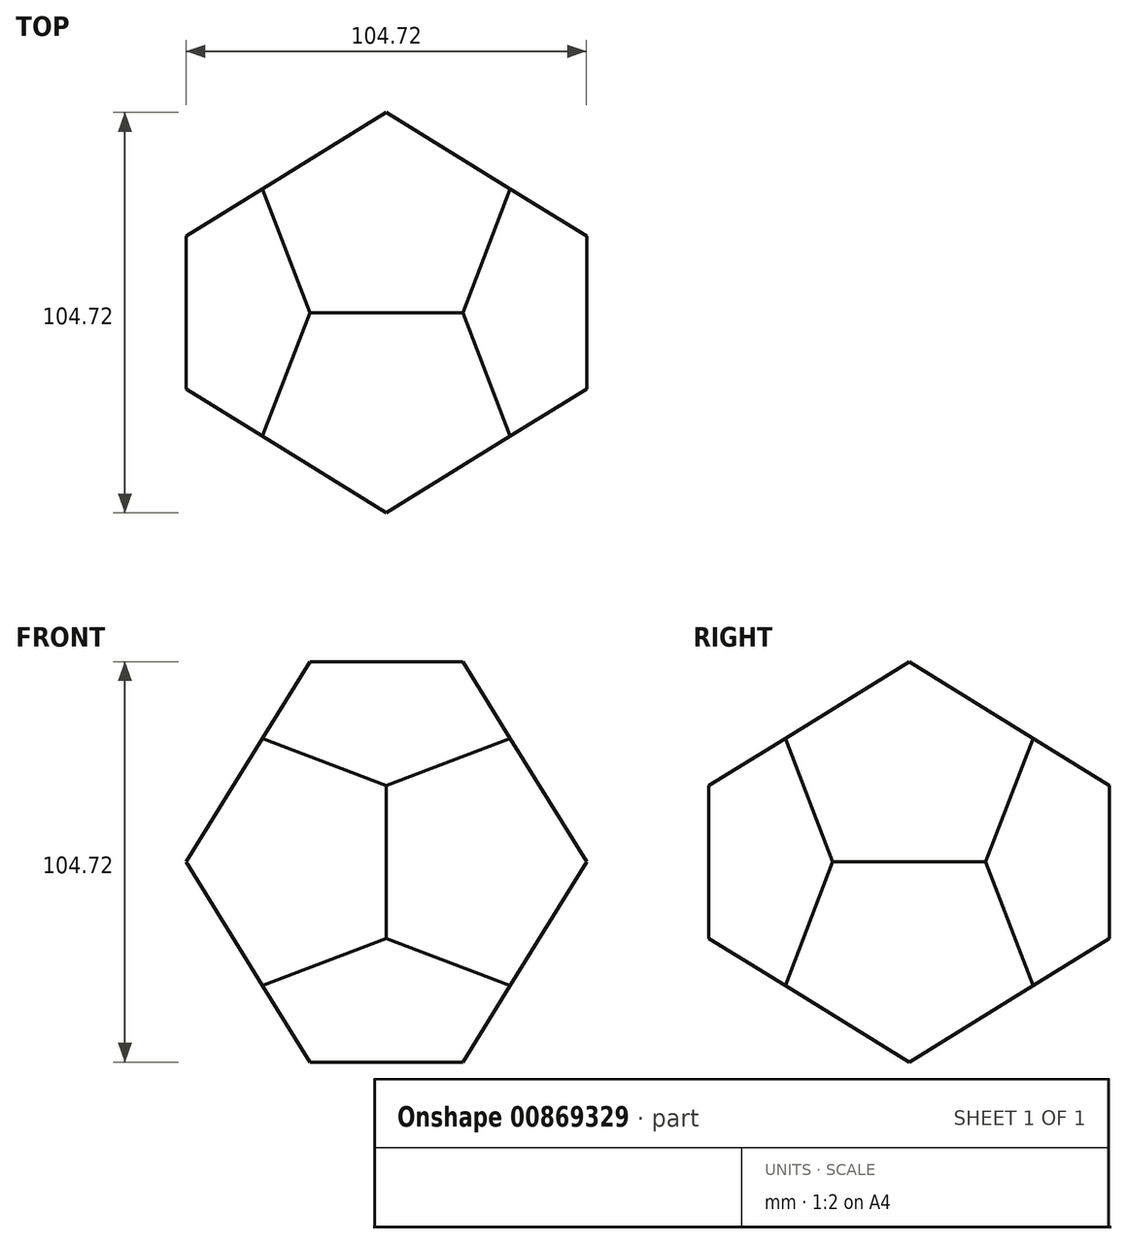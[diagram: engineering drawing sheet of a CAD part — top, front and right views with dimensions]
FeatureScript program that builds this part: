
annotation { "Feature Type Name" : "Feature", "Feature Type Description" : "" }
export const myFeature = defineFeature(function(context is Context, id is Id, definition is map)
    precondition{}
    {
        {
            assignVariable(context, id + "F0", {"name" : "lado", "anyValue" : 40});
        }
        {
            assignVariable(context, id + "F1", {"name" : "ladoSeccion", "anyValue" : (1 + sqrt(5)) / 2 * getVariable(context, 'lado')});
        }
        {
            var Q0;
            Q0=qCreatedBy(makeId("Top.planeOp"),FACE);
            var sketch = newSketch(context, id + "F2", { "sketchPlane" : qUnion([Q0])});
            skLineSegment(sketch, "E0.bottom", {"start": v(-32.36, 32.36) * mm, "end": v(32.36, 32.36) * mm});
            skLineSegment(sketch, "E0.top", {"start": v(-32.36, -32.36) * mm, "end": v(32.36, -32.36) * mm});
            skLineSegment(sketch, "E0.left", {"start": v(-32.36, 32.36) * mm, "end": v(-32.36, -32.36) * mm});
            skLineSegment(sketch, "E0.right", {"start": v(32.36, 32.36) * mm, "end": v(32.36, -32.36) * mm});
            skSolve(sketch);
        }
        {
            var Q0;
            Q0=makeQuery(id+"F2.imprint","IMPRINT",FACE,{"disambiguationData":[TD([[makeQuery(id+"F2.imprint","IMPRINT",EDGE,{"derivedFrom":sQuery(id+"F2.wireOp",EDGE,"E0.bottom")}),-1.0]])]});
            extrude(context, id + "F3", {"entities" : qUnion([Q0]), "depth" : (getVariable(context, 'ladoSeccion')) * mm, "offsetDistance" : 25 * mm, "symmetric" : true});
        }
        {
            var Q0;
            Q0=makeQuery(id+"F3.opExtrude","SWEPT_FACE",FACE,{"disambiguationData":[OSD([sQuery(id+"F2.wireOp",EDGE,"E0.bottom")])]});
            var sketch = newSketch(context, id + "F4", { "sketchPlane" : qUnion([Q0])});
            skLineSegment(sketch, "E1.0", {"start": v(32.36, 32.36) * mm, "end": v(-32.36, 32.36) * mm});
            skLineSegment(sketch, "E2.0", {"start": v(-32.36, 32.36) * mm, "end": v(-32.36, -32.36) * mm});
            skLineSegment(sketch, "E3.0", {"start": v(32.36, -32.36) * mm, "end": v(-32.36, -32.36) * mm});
            skLineSegment(sketch, "E4.0", {"start": v(32.36, 32.36) * mm, "end": v(32.36, -32.36) * mm});
            skLineSegment(sketch, "E5", {"start": v(-32.36, 32.36) * mm, "end": v(32.36, -32.36) * mm});
            skLineSegment(sketch, "E6", {"start": v(32.36, 32.36) * mm, "end": v(-32.36, -32.36) * mm});
            skPoint(sketch, "E7", {"position": v(0, 0) * mm});
            skSolve(sketch);
        }
        {
            var Q0;
            Q0=qCreatedBy(makeId("Right.planeOp"),FACE);
            var sketch = newSketch(context, id + "F5", { "sketchPlane" : qUnion([Q0])});
            skLineSegment(sketch, "E8.0", {"start": v(32.36, 32.36) * mm, "end": v(32.36, -32.36) * mm});
            skLineSegment(sketch, "E9", {"start": v(32.36, 0) * mm, "end": v(52.36, 0) * mm});
            skPoint(sketch, "E9.endSnap0", {"position": v(32.36, 0) * mm});
            skLineSegment(sketch, "E10", {"start": v(52.36, -20) * mm, "end": v(52.36, 20) * mm});
            skSolve(sketch);
        }
        {
            var Q1;
            {var subQ0=sQuery(id+"F4.wireOp",EDGE,"E2.0");Q1=makeQuery(id+"F4.imprint","IMPRINT",FACE,{"disambiguationData":[TD([[makeQuery(id+"F4.imprint","IMPRINT",EDGE,{"derivedFrom":subQ0}),1.0]])]});}
            var Q2;
            Q2=sQuery(id+"F5.wireOp",VERTEX,"E9.end");
            loft(context, id + "F6", {"operationType" : NewBodyOperationType.ADD, "sheetProfilesArray" : [{ "sheetProfileEntities" : qUnion([Q1]) }, { "sheetProfileEntities" : qUnion([Q2]) }]});
        }
        {
            var Q1;
            {var subQ0=sQuery(id+"F4.wireOp",EDGE,"E1.0");Q1=makeQuery(id+"F4.imprint","IMPRINT",FACE,{"disambiguationData":[TD([[makeQuery(id+"F4.imprint","IMPRINT",EDGE,{"derivedFrom":subQ0}),1.0]])]});}
            var Q2;
            Q2=sQuery(id+"F5.wireOp",VERTEX,"E10.end");
            loft(context, id + "F7", {"operationType" : NewBodyOperationType.ADD, "sheetProfilesArray" : [{ "sheetProfileEntities" : qUnion([Q1]) }, { "sheetProfileEntities" : qUnion([Q2]) }]});
        }
        {
            var Q1;
            {var subQ0=sQuery(id+"F4.wireOp",EDGE,"E3.0");Q1=makeQuery(id+"F4.imprint","IMPRINT",FACE,{"disambiguationData":[TD([[makeQuery(id+"F4.imprint","IMPRINT",EDGE,{"derivedFrom":subQ0}),-1.0]])]});}
            var Q2;
            Q2=sQuery(id+"F5.wireOp",VERTEX,"E10.start");
            loft(context, id + "F8", {"operationType" : NewBodyOperationType.ADD, "sheetProfilesArray" : [{ "sheetProfileEntities" : qUnion([Q1]) }, { "sheetProfileEntities" : qUnion([Q2]) }]});
        }
        {
            var Q1;
            Q1=makeQuery(id+"F6.opLoft","SWEPT_FACE",FACE,{"disambiguationData":[OSD([sQuery(id+"F4.wireOp",EDGE,"E2.0"),sQuery(id+"F4.wireOp",EDGE,"E3.0"),sQuery(id+"F4.wireOp",EDGE,"E5"),sQuery(id+"F4.wireOp",EDGE,"E6")])]});
            var Q2;
            Q2=sQuery(id+"F5.wireOp",VERTEX,"E10.start");
            loft(context, id + "F9", {"operationType" : NewBodyOperationType.ADD, "sheetProfilesArray" : [{ "sheetProfileEntities" : qUnion([Q1]) }, { "sheetProfileEntities" : qUnion([Q2]) }]});
        }
        {
            var Q1;
            Q1=makeQuery(id+"F6.opLoft","SWEPT_FACE",FACE,{"disambiguationData":[OSD([sQuery(id+"F4.wireOp",EDGE,"E1.0"),sQuery(id+"F4.wireOp",EDGE,"E2.0"),sQuery(id+"F4.wireOp",EDGE,"E5"),sQuery(id+"F4.wireOp",EDGE,"E6")])]});
            var Q2;
            Q2=sQuery(id+"F5.wireOp",VERTEX,"E10.end");
            loft(context, id + "F10", {"operationType" : NewBodyOperationType.ADD, "sheetProfilesArray" : [{ "sheetProfileEntities" : qUnion([Q1]) }, { "sheetProfileEntities" : qUnion([Q2]) }]});
        }
        {
            var Q1;
            {var subQ0=sQuery(id+"F4.wireOp",EDGE,"E4.0");Q1=makeQuery(id+"F4.imprint","IMPRINT",FACE,{"disambiguationData":[TD([[makeQuery(id+"F4.imprint","IMPRINT",EDGE,{"derivedFrom":subQ0}),-1.0]])]});}
            var Q2;
            Q2=sQuery(id+"F5.wireOp",VERTEX,"E10.start");
            loft(context, id + "F11", {"operationType" : NewBodyOperationType.ADD, "sheetProfilesArray" : [{ "sheetProfileEntities" : qUnion([Q1]) }, { "sheetProfileEntities" : qUnion([Q2]) }]});
        }
        {
            var Q1;
            Q1=makeQuery(id+"F11.opLoft","SWEPT_FACE",FACE,{"disambiguationData":[OSD([sQuery(id+"F4.wireOp",EDGE,"E1.0"),sQuery(id+"F4.wireOp",EDGE,"E4.0"),sQuery(id+"F4.wireOp",EDGE,"E5"),sQuery(id+"F4.wireOp",EDGE,"E6")])]});
            var Q2;
            Q2=sQuery(id+"F5.wireOp",VERTEX,"E10.end");
            loft(context, id + "F12", {"operationType" : NewBodyOperationType.ADD, "sheetProfilesArray" : [{ "sheetProfileEntities" : qUnion([Q1]) }, { "sheetProfileEntities" : qUnion([Q2]) }]});
        }
        {
            var Q0;
            Q0=makeQuery(id+"F3.opExtrude","CAP_FACE",FACE,{"disambiguationData":[OSD([sQuery(id+"F2.wireOp",EDGE,"E0.bottom"),sQuery(id+"F2.wireOp",EDGE,"E0.top"),sQuery(id+"F2.wireOp",EDGE,"E0.left"),sQuery(id+"F2.wireOp",EDGE,"E0.right")])],"isStart":false});
            var sketch = newSketch(context, id + "F13", { "sketchPlane" : qUnion([Q0])});
            skLineSegment(sketch, "E11.0", {"start": v(32.36, 32.36) * mm, "end": v(32.36, -32.36) * mm});
            skLineSegment(sketch, "E12.0", {"start": v(-32.36, 32.36) * mm, "end": v(32.36, 32.36) * mm});
            skLineSegment(sketch, "E13.0", {"start": v(-32.36, -32.36) * mm, "end": v(32.36, -32.36) * mm});
            skLineSegment(sketch, "E14.0", {"start": v(-32.36, 32.36) * mm, "end": v(-32.36, -32.36) * mm});
            skLineSegment(sketch, "E15", {"start": v(32.36, -32.36) * mm, "end": v(-32.36, 32.36) * mm});
            skLineSegment(sketch, "E16", {"start": v(-32.36, -32.36) * mm, "end": v(32.36, 32.36) * mm});
            skPoint(sketch, "E17", {"position": v(0, 0) * mm});
            skSolve(sketch);
        }
        {
            var Q0;
            Q0=qCreatedBy(makeId("Front.planeOp"),FACE);
            var sketch = newSketch(context, id + "F14", { "sketchPlane" : qUnion([Q0])});
            skLineSegment(sketch, "E18.0", {"start": v(32.36, 32.36) * mm, "end": v(-32.36, 32.36) * mm});
            skLineSegment(sketch, "E19", {"start": v(0, 32.36) * mm, "end": v(0, 52.36) * mm});
            skPoint(sketch, "E19.endSnap0", {"position": v(0, 32.36) * mm});
            skLineSegment(sketch, "E20", {"start": v(20, 52.36) * mm, "end": v(-20, 52.36) * mm});
            skSolve(sketch);
        }
        {
            var Q1;
            {var subQ0=sQuery(id+"F13.wireOp",EDGE,"E13.0");Q1=makeQuery(id+"F13.imprint","IMPRINT",FACE,{"disambiguationData":[TD([[makeQuery(id+"F13.imprint","IMPRINT",EDGE,{"derivedFrom":subQ0}),1.0]])]});}
            var Q2;
            Q2=sQuery(id+"F14.wireOp",VERTEX,"E19.end");
            loft(context, id + "F15", {"operationType" : NewBodyOperationType.ADD, "sheetProfilesArray" : [{ "sheetProfileEntities" : qUnion([Q1]) }, { "sheetProfileEntities" : qUnion([Q2]) }]});
        }
        {
            var Q1;
            {var subQ0=sQuery(id+"F13.wireOp",EDGE,"E11.0");Q1=makeQuery(id+"F13.imprint","IMPRINT",FACE,{"disambiguationData":[TD([[makeQuery(id+"F13.imprint","IMPRINT",EDGE,{"derivedFrom":subQ0}),-1.0]])]});}
            var Q2;
            Q2=sQuery(id+"F14.wireOp",VERTEX,"E20.start");
            loft(context, id + "F16", {"operationType" : NewBodyOperationType.ADD, "sheetProfilesArray" : [{ "sheetProfileEntities" : qUnion([Q1]) }, { "sheetProfileEntities" : qUnion([Q2]) }]});
        }
        {
            var Q1;
            {var subQ0=sQuery(id+"F13.wireOp",EDGE,"E14.0");Q1=makeQuery(id+"F13.imprint","IMPRINT",FACE,{"disambiguationData":[TD([[makeQuery(id+"F13.imprint","IMPRINT",EDGE,{"derivedFrom":subQ0}),1.0]])]});}
            var Q2;
            Q2=sQuery(id+"F14.wireOp",VERTEX,"E20.end");
            loft(context, id + "F17", {"operationType" : NewBodyOperationType.ADD, "sheetProfilesArray" : [{ "sheetProfileEntities" : qUnion([Q1]) }, { "sheetProfileEntities" : qUnion([Q2]) }]});
        }
        {
            var Q1;
            Q1=makeQuery(id+"F17.opLoft","SWEPT_FACE",FACE,{"disambiguationData":[OSD([sQuery(id+"F13.wireOp",EDGE,"E13.0"),sQuery(id+"F13.wireOp",EDGE,"E14.0"),sQuery(id+"F13.wireOp",EDGE,"E15"),sQuery(id+"F13.wireOp",EDGE,"E16")])]});
            var Q2;
            Q2=sQuery(id+"F14.wireOp",VERTEX,"E19.end");
            loft(context, id + "F18", {"operationType" : NewBodyOperationType.ADD, "sheetProfilesArray" : [{ "sheetProfileEntities" : qUnion([Q1]) }, { "sheetProfileEntities" : qUnion([Q2]) }]});
        }
        {
            var Q1;
            Q1=makeQuery(id+"F16.opLoft","SWEPT_FACE",FACE,{"disambiguationData":[OSD([sQuery(id+"F13.wireOp",EDGE,"E11.0"),sQuery(id+"F13.wireOp",EDGE,"E13.0"),sQuery(id+"F13.wireOp",EDGE,"E15"),sQuery(id+"F13.wireOp",EDGE,"E16")])]});
            var Q2;
            Q2=sQuery(id+"F14.wireOp",VERTEX,"E19.end");
            loft(context, id + "F19", {"operationType" : NewBodyOperationType.ADD, "sheetProfilesArray" : [{ "sheetProfileEntities" : qUnion([Q1]) }, { "sheetProfileEntities" : qUnion([Q2]) }]});
        }
        {
            var Q1;
            {var subQ0=sQuery(id+"F13.wireOp",EDGE,"E12.0");Q1=makeQuery(id+"F13.imprint","IMPRINT",FACE,{"disambiguationData":[TD([[makeQuery(id+"F13.imprint","IMPRINT",EDGE,{"derivedFrom":subQ0}),-1.0]])]});}
            var Q2;
            Q2=sQuery(id+"F14.wireOp",VERTEX,"E20.start");
            loft(context, id + "F20", {"operationType" : NewBodyOperationType.ADD, "sheetProfilesArray" : [{ "sheetProfileEntities" : qUnion([Q1]) }, { "sheetProfileEntities" : qUnion([Q2]) }]});
        }
        {
            var Q1;
            Q1=makeQuery(id+"F20.opLoft","SWEPT_FACE",FACE,{"disambiguationData":[OSD([sQuery(id+"F13.wireOp",EDGE,"E12.0"),sQuery(id+"F13.wireOp",EDGE,"E14.0"),sQuery(id+"F13.wireOp",EDGE,"E15"),sQuery(id+"F13.wireOp",EDGE,"E16")])]});
            var Q2;
            Q2=sQuery(id+"F14.wireOp",VERTEX,"E20.end");
            loft(context, id + "F21", {"operationType" : NewBodyOperationType.ADD, "sheetProfilesArray" : [{ "sheetProfileEntities" : qUnion([Q1]) }, { "sheetProfileEntities" : qUnion([Q2]) }]});
        }
        {
            var Q0;
            Q0=makeQuery(id+"F3.opExtrude","SWEPT_FACE",FACE,{"disambiguationData":[OSD([sQuery(id+"F2.wireOp",EDGE,"E0.top")])]});
            var sketch = newSketch(context, id + "F22", { "sketchPlane" : qUnion([Q0])});
            skLineSegment(sketch, "E21.0", {"start": v(32.36, 32.36) * mm, "end": v(32.36, -32.36) * mm});
            skLineSegment(sketch, "E22.0", {"start": v(-32.36, 32.36) * mm, "end": v(32.36, 32.36) * mm});
            skLineSegment(sketch, "E23.0", {"start": v(-32.36, 32.36) * mm, "end": v(-32.36, -32.36) * mm});
            skLineSegment(sketch, "E24.0", {"start": v(-32.36, -32.36) * mm, "end": v(32.36, -32.36) * mm});
            skLineSegment(sketch, "E25", {"start": v(32.36, 32.36) * mm, "end": v(-32.36, -32.36) * mm});
            skLineSegment(sketch, "E26", {"start": v(32.36, -32.36) * mm, "end": v(-32.36, 32.36) * mm});
            skSolve(sketch);
        }
        {
            var Q0;
            Q0=qCreatedBy(makeId("Right.planeOp"),FACE);
            var sketch = newSketch(context, id + "F23", { "sketchPlane" : qUnion([Q0])});
            skLineSegment(sketch, "E27.0", {"start": v(-32.36, 32.36) * mm, "end": v(-32.36, -32.36) * mm});
            skLineSegment(sketch, "E28", {"start": v(-32.36, 0) * mm, "end": v(-52.36, 0) * mm});
            skLineSegment(sketch, "E29", {"start": v(-52.36, 20) * mm, "end": v(-52.36, -20) * mm});
            skSolve(sketch);
        }
        {
            var Q1;
            Q1=sQuery(id+"F23.wireOp",VERTEX,"E29.start");
            var Q2;
            {var subQ0=sQuery(id+"F22.wireOp",EDGE,"E23.0");Q2=makeQuery(id+"F22.imprint","IMPRINT",FACE,{"disambiguationData":[TD([[makeQuery(id+"F22.imprint","IMPRINT",EDGE,{"derivedFrom":subQ0}),1.0]])]});}
            loft(context, id + "F24", {"operationType" : NewBodyOperationType.ADD, "sheetProfilesArray" : [{ "sheetProfileEntities" : qUnion([Q1]) }, { "sheetProfileEntities" : qUnion([Q2]) }]});
        }
        {
            var Q1;
            {var subQ0=sQuery(id+"F22.wireOp",EDGE,"E24.0");Q1=makeQuery(id+"F22.imprint","IMPRINT",FACE,{"disambiguationData":[TD([[makeQuery(id+"F22.imprint","IMPRINT",EDGE,{"derivedFrom":subQ0}),1.0]])]});}
            var Q2;
            Q2=sQuery(id+"F23.wireOp",VERTEX,"E29.end");
            loft(context, id + "F25", {"operationType" : NewBodyOperationType.ADD, "sheetProfilesArray" : [{ "sheetProfileEntities" : qUnion([Q1]) }, { "sheetProfileEntities" : qUnion([Q2]) }]});
        }
        {
            var Q1;
            {var subQ0=sQuery(id+"F22.wireOp",EDGE,"E21.0");Q1=makeQuery(id+"F22.imprint","IMPRINT",FACE,{"disambiguationData":[TD([[makeQuery(id+"F22.imprint","IMPRINT",EDGE,{"derivedFrom":subQ0}),-1.0]])]});}
            var Q2;
            Q2=sQuery(id+"F23.wireOp",VERTEX,"E28.end");
            loft(context, id + "F26", {"operationType" : NewBodyOperationType.ADD, "sheetProfilesArray" : [{ "sheetProfileEntities" : qUnion([Q1]) }, { "sheetProfileEntities" : qUnion([Q2]) }]});
        }
        {
            var Q1;
            {var subQ0=sQuery(id+"F22.wireOp",EDGE,"E22.0");Q1=makeQuery(id+"F22.imprint","IMPRINT",FACE,{"disambiguationData":[TD([[makeQuery(id+"F22.imprint","IMPRINT",EDGE,{"derivedFrom":subQ0}),-1.0]])]});}
            var Q2;
            Q2=sQuery(id+"F23.wireOp",VERTEX,"E29.start");
            loft(context, id + "F27", {"operationType" : NewBodyOperationType.ADD, "sheetProfilesArray" : [{ "sheetProfileEntities" : qUnion([Q1]) }, { "sheetProfileEntities" : qUnion([Q2]) }]});
        }
        {
            var Q1;
            Q1=makeQuery(id+"F26.opLoft","SWEPT_FACE",FACE,{"disambiguationData":[OSD([sQuery(id+"F22.wireOp",EDGE,"E21.0"),sQuery(id+"F22.wireOp",EDGE,"E24.0"),sQuery(id+"F22.wireOp",EDGE,"E25"),sQuery(id+"F22.wireOp",EDGE,"E26")])]});
            var Q2;
            Q2=sQuery(id+"F23.wireOp",VERTEX,"E29.end");
            loft(context, id + "F28", {"operationType" : NewBodyOperationType.ADD, "sheetProfilesArray" : [{ "sheetProfileEntities" : qUnion([Q1]) }, { "sheetProfileEntities" : qUnion([Q2]) }]});
        }
        {
            var Q1;
            Q1=makeQuery(id+"F26.opLoft","SWEPT_FACE",FACE,{"disambiguationData":[OSD([sQuery(id+"F22.wireOp",EDGE,"E21.0"),sQuery(id+"F22.wireOp",EDGE,"E22.0"),sQuery(id+"F22.wireOp",EDGE,"E25"),sQuery(id+"F22.wireOp",EDGE,"E26")])]});
            var Q2;
            Q2=sQuery(id+"F23.wireOp",VERTEX,"E29.start");
            loft(context, id + "F29", {"operationType" : NewBodyOperationType.ADD, "sheetProfilesArray" : [{ "sheetProfileEntities" : qUnion([Q1]) }, { "sheetProfileEntities" : qUnion([Q2]) }]});
        }
        {
            var Q1;
            {var subQ0=sQuery(id+"F22.wireOp",EDGE,"E26");var subQ1=sQuery(id+"F22.wireOp",EDGE,"E25");Q1=makeQuery(id+"F27.boolean.opBoolean","MERGE",FACE,{"derivedFrom":[makeQuery(id+"F24.opLoft","SWEPT_FACE",FACE,{"disambiguationData":[OSD([sQuery(id+"F22.wireOp",EDGE,"E23.0"),sQuery(id+"F22.wireOp",EDGE,"E24.0"),subQ1,subQ0])]}),makeQuery(id+"F27.opLoft","SWEPT_FACE",FACE,{"disambiguationData":[OSD([sQuery(id+"F22.wireOp",EDGE,"E21.0"),sQuery(id+"F22.wireOp",EDGE,"E22.0"),subQ1,subQ0])]})]});}
            var Q2;
            Q2=sQuery(id+"F23.wireOp",VERTEX,"E29.end");
            loft(context, id + "F30", {"operationType" : NewBodyOperationType.ADD, "sheetProfilesArray" : [{ "sheetProfileEntities" : qUnion([Q1]) }, { "sheetProfileEntities" : qUnion([Q2]) }]});
        }
        {
            var Q0;
            Q0=makeQuery(id+"F3.opExtrude","SWEPT_FACE",FACE,{"disambiguationData":[OSD([sQuery(id+"F2.wireOp",EDGE,"E0.right")])]});
            var sketch = newSketch(context, id + "F31", { "sketchPlane" : qUnion([Q0])});
            skLineSegment(sketch, "E30.0", {"start": v(32.36, 32.36) * mm, "end": v(-32.36, 32.36) * mm});
            skLineSegment(sketch, "E31.0", {"start": v(-32.36, 32.36) * mm, "end": v(-32.36, -32.36) * mm});
            skLineSegment(sketch, "E32.0", {"start": v(32.36, -32.36) * mm, "end": v(-32.36, -32.36) * mm});
            skLineSegment(sketch, "E33.0", {"start": v(32.36, 32.36) * mm, "end": v(32.36, -32.36) * mm});
            skLineSegment(sketch, "E34", {"start": v(32.36, 32.36) * mm, "end": v(-32.36, -32.36) * mm});
            skLineSegment(sketch, "E35", {"start": v(-32.36, 32.36) * mm, "end": v(32.36, -32.36) * mm});
            skSolve(sketch);
        }
        {
            var Q0;
            Q0=qCreatedBy(makeId("Top.planeOp"),FACE);
            var sketch = newSketch(context, id + "F32", { "sketchPlane" : qUnion([Q0])});
            skLineSegment(sketch, "E36.0", {"start": v(32.36, -32.36) * mm, "end": v(32.36, 32.36) * mm});
            skLineSegment(sketch, "E37", {"start": v(32.36, 0) * mm, "end": v(52.36, 0) * mm});
            skLineSegment(sketch, "E38", {"start": v(52.36, -20) * mm, "end": v(52.36, 20) * mm});
            skSolve(sketch);
        }
        {
            var Q1;
            {var subQ0=sQuery(id+"F31.wireOp",EDGE,"E31.0");Q1=makeQuery(id+"F31.imprint","IMPRINT",FACE,{"disambiguationData":[TD([[makeQuery(id+"F31.imprint","IMPRINT",EDGE,{"derivedFrom":subQ0}),1.0]])]});}
            var Q2;
            Q2=sQuery(id+"F32.wireOp",VERTEX,"E38.start");
            loft(context, id + "F33", {"operationType" : NewBodyOperationType.ADD, "sheetProfilesArray" : [{ "sheetProfileEntities" : qUnion([Q1]) }, { "sheetProfileEntities" : qUnion([Q2]) }]});
        }
        {
            var Q1;
            {var subQ0=sQuery(id+"F31.wireOp",EDGE,"E32.0");Q1=makeQuery(id+"F31.imprint","IMPRINT",FACE,{"disambiguationData":[TD([[makeQuery(id+"F31.imprint","IMPRINT",EDGE,{"derivedFrom":subQ0}),-1.0]])]});}
            var Q2;
            Q2=sQuery(id+"F32.wireOp",VERTEX,"E38.end");
            loft(context, id + "F34", {"operationType" : NewBodyOperationType.ADD, "sheetProfilesArray" : [{ "sheetProfileEntities" : qUnion([Q1]) }, { "sheetProfileEntities" : qUnion([Q2]) }]});
        }
        {
            var Q1;
            {var subQ0=sQuery(id+"F31.wireOp",EDGE,"E30.0");Q1=makeQuery(id+"F31.imprint","IMPRINT",FACE,{"disambiguationData":[TD([[makeQuery(id+"F31.imprint","IMPRINT",EDGE,{"derivedFrom":subQ0}),1.0]])]});}
            var Q2;
            Q2=sQuery(id+"F32.wireOp",VERTEX,"E38.start");
            loft(context, id + "F35", {"operationType" : NewBodyOperationType.ADD, "sheetProfilesArray" : [{ "sheetProfileEntities" : qUnion([Q1]) }, { "sheetProfileEntities" : qUnion([Q2]) }]});
        }
        {
            var Q1;
            {var subQ0=sQuery(id+"F31.wireOp",EDGE,"E33.0");Q1=makeQuery(id+"F31.imprint","IMPRINT",FACE,{"disambiguationData":[TD([[makeQuery(id+"F31.imprint","IMPRINT",EDGE,{"derivedFrom":subQ0}),-1.0]])]});}
            var Q2;
            Q2=sQuery(id+"F32.wireOp",VERTEX,"E38.end");
            loft(context, id + "F36", {"operationType" : NewBodyOperationType.ADD, "sheetProfilesArray" : [{ "sheetProfileEntities" : qUnion([Q1]) }, { "sheetProfileEntities" : qUnion([Q2]) }]});
        }
        {
            var Q1;
            {var subQ0=sQuery(id+"F31.wireOp",EDGE,"E35");var subQ1=sQuery(id+"F31.wireOp",EDGE,"E34");Q1=makeQuery(id+"F36.boolean.opBoolean","MERGE",FACE,{"derivedFrom":[makeQuery(id+"F34.opLoft","SWEPT_FACE",FACE,{"disambiguationData":[OSD([sQuery(id+"F31.wireOp",EDGE,"E31.0"),sQuery(id+"F31.wireOp",EDGE,"E32.0"),subQ1,subQ0])]}),makeQuery(id+"F36.opLoft","SWEPT_FACE",FACE,{"disambiguationData":[OSD([sQuery(id+"F31.wireOp",EDGE,"E30.0"),sQuery(id+"F31.wireOp",EDGE,"E33.0"),subQ1,subQ0])]})]});}
            var Q2;
            Q2=sQuery(id+"F32.wireOp",VERTEX,"E38.start");
            loft(context, id + "F37", {"operationType" : NewBodyOperationType.ADD, "sheetProfilesArray" : [{ "sheetProfileEntities" : qUnion([Q1]) }, { "sheetProfileEntities" : qUnion([Q2]) }]});
        }
        {
            var Q0;
            Q0=makeQuery(id+"F3.opExtrude","SWEPT_FACE",FACE,{"disambiguationData":[OSD([sQuery(id+"F2.wireOp",EDGE,"E0.left")])]});
            var sketch = newSketch(context, id + "F38", { "sketchPlane" : qUnion([Q0])});
            skLineSegment(sketch, "E39.0", {"start": v(-32.36, 32.36) * mm, "end": v(-32.36, -32.36) * mm});
            skLineSegment(sketch, "E40.0", {"start": v(-32.36, 32.36) * mm, "end": v(32.36, 32.36) * mm});
            skLineSegment(sketch, "E41.0", {"start": v(32.36, 32.36) * mm, "end": v(32.36, -32.36) * mm});
            skLineSegment(sketch, "E42.0", {"start": v(-32.36, -32.36) * mm, "end": v(32.36, -32.36) * mm});
            skLineSegment(sketch, "E43", {"start": v(-32.36, 32.36) * mm, "end": v(32.36, -32.36) * mm});
            skLineSegment(sketch, "E44", {"start": v(32.36, 32.36) * mm, "end": v(-32.36, -32.36) * mm});
            skSolve(sketch);
        }
        {
            var Q0;
            Q0=qCreatedBy(makeId("Top.planeOp"),FACE);
            var sketch = newSketch(context, id + "F39", { "sketchPlane" : qUnion([Q0])});
            skLineSegment(sketch, "E45.0", {"start": v(-32.36, 32.36) * mm, "end": v(-32.36, -32.36) * mm});
            skLineSegment(sketch, "E46", {"start": v(-32.36, 0) * mm, "end": v(-52.36, 0) * mm});
            skLineSegment(sketch, "E47", {"start": v(-52.36, 20) * mm, "end": v(-52.36, -20) * mm});
            skSolve(sketch);
        }
        {
            var Q1;
            {var subQ0=sQuery(id+"F38.wireOp",EDGE,"E39.0");Q1=makeQuery(id+"F38.imprint","IMPRINT",FACE,{"disambiguationData":[TD([[makeQuery(id+"F38.imprint","IMPRINT",EDGE,{"derivedFrom":subQ0}),1.0]])]});}
            var Q2;
            Q2=sQuery(id+"F39.wireOp",VERTEX,"E47.start");
            loft(context, id + "F40", {"operationType" : NewBodyOperationType.ADD, "sheetProfilesArray" : [{ "sheetProfileEntities" : qUnion([Q1]) }, { "sheetProfileEntities" : qUnion([Q2]) }]});
        }
        {
            var Q1;
            {var subQ0=sQuery(id+"F38.wireOp",EDGE,"E42.0");Q1=makeQuery(id+"F38.imprint","IMPRINT",FACE,{"disambiguationData":[TD([[makeQuery(id+"F38.imprint","IMPRINT",EDGE,{"derivedFrom":subQ0}),1.0]])]});}
            var Q2;
            Q2=sQuery(id+"F39.wireOp",VERTEX,"E46.end");
            loft(context, id + "F41", {"operationType" : NewBodyOperationType.ADD, "sheetProfilesArray" : [{ "sheetProfileEntities" : qUnion([Q1]) }, { "sheetProfileEntities" : qUnion([Q2]) }]});
        }
        {
            var Q1;
            {var subQ0=sQuery(id+"F38.wireOp",EDGE,"E41.0");Q1=makeQuery(id+"F38.imprint","IMPRINT",FACE,{"disambiguationData":[TD([[makeQuery(id+"F38.imprint","IMPRINT",EDGE,{"derivedFrom":subQ0}),-1.0]])]});}
            var Q2;
            Q2=sQuery(id+"F39.wireOp",VERTEX,"E47.end");
            loft(context, id + "F42", {"operationType" : NewBodyOperationType.ADD, "sheetProfilesArray" : [{ "sheetProfileEntities" : qUnion([Q1]) }, { "sheetProfileEntities" : qUnion([Q2]) }]});
        }
        {
            var Q1;
            {var subQ0=sQuery(id+"F38.wireOp",EDGE,"E40.0");Q1=makeQuery(id+"F38.imprint","IMPRINT",FACE,{"disambiguationData":[TD([[makeQuery(id+"F38.imprint","IMPRINT",EDGE,{"derivedFrom":subQ0}),-1.0]])]});}
            var Q2;
            Q2=sQuery(id+"F39.wireOp",VERTEX,"E47.start");
            loft(context, id + "F43", {"operationType" : NewBodyOperationType.ADD, "sheetProfilesArray" : [{ "sheetProfileEntities" : qUnion([Q1]) }, { "sheetProfileEntities" : qUnion([Q2]) }]});
        }
        {
            var Q1;
            Q1=makeQuery(id+"F42.opLoft","SWEPT_FACE",FACE,{"disambiguationData":[OSD([sQuery(id+"F38.wireOp",EDGE,"E41.0"),sQuery(id+"F38.wireOp",EDGE,"E42.0"),sQuery(id+"F38.wireOp",EDGE,"E43"),sQuery(id+"F38.wireOp",EDGE,"E44")])]});
            var Q2;
            Q2=sQuery(id+"F39.wireOp",VERTEX,"E46.end");
            loft(context, id + "F44", {"operationType" : NewBodyOperationType.ADD, "sheetProfilesArray" : [{ "sheetProfileEntities" : qUnion([Q1]) }, { "sheetProfileEntities" : qUnion([Q2]) }]});
        }
        {
            var Q1;
            Q1=makeQuery(id+"F41.opLoft","SWEPT_FACE",FACE,{"disambiguationData":[OSD([sQuery(id+"F38.wireOp",EDGE,"E39.0"),sQuery(id+"F38.wireOp",EDGE,"E42.0"),sQuery(id+"F38.wireOp",EDGE,"E43"),sQuery(id+"F38.wireOp",EDGE,"E44")])]});
            var Q2;
            Q2=sQuery(id+"F39.wireOp",VERTEX,"E47.start");
            loft(context, id + "F45", {"operationType" : NewBodyOperationType.ADD, "sheetProfilesArray" : [{ "sheetProfileEntities" : qUnion([Q1]) }, { "sheetProfileEntities" : qUnion([Q2]) }]});
        }
        {
            var Q1;
            {var subQ0=sQuery(id+"F38.wireOp",EDGE,"E44");var subQ1=sQuery(id+"F38.wireOp",EDGE,"E43");Q1=makeQuery(id+"F43.boolean.opBoolean","MERGE",FACE,{"derivedFrom":[makeQuery(id+"F40.opLoft","SWEPT_FACE",FACE,{"disambiguationData":[OSD([sQuery(id+"F38.wireOp",EDGE,"E39.0"),sQuery(id+"F38.wireOp",EDGE,"E42.0"),subQ1,subQ0])]}),makeQuery(id+"F43.opLoft","SWEPT_FACE",FACE,{"disambiguationData":[OSD([sQuery(id+"F38.wireOp",EDGE,"E40.0"),sQuery(id+"F38.wireOp",EDGE,"E41.0"),subQ1,subQ0])]})]});}
            var Q2;
            Q2=sQuery(id+"F39.wireOp",VERTEX,"E47.end");
            loft(context, id + "F46", {"operationType" : NewBodyOperationType.ADD, "sheetProfilesArray" : [{ "sheetProfileEntities" : qUnion([Q1]) }, { "sheetProfileEntities" : qUnion([Q2]) }]});
        }
        {
            var Q0;
            Q0=makeQuery(id+"F3.opExtrude","CAP_FACE",FACE,{"disambiguationData":[OSD([sQuery(id+"F2.wireOp",EDGE,"E0.bottom"),sQuery(id+"F2.wireOp",EDGE,"E0.top"),sQuery(id+"F2.wireOp",EDGE,"E0.left"),sQuery(id+"F2.wireOp",EDGE,"E0.right")])],"isStart":true});
            var sketch = newSketch(context, id + "F47", { "sketchPlane" : qUnion([Q0])});
            skLineSegment(sketch, "E48.0", {"start": v(-32.36, 32.36) * mm, "end": v(32.36, 32.36) * mm});
            skLineSegment(sketch, "E49.0", {"start": v(32.36, -32.36) * mm, "end": v(32.36, 32.36) * mm});
            skLineSegment(sketch, "E50.0", {"start": v(-32.36, -32.36) * mm, "end": v(-32.36, 32.36) * mm});
            skLineSegment(sketch, "E51.0", {"start": v(-32.36, -32.36) * mm, "end": v(32.36, -32.36) * mm});
            skLineSegment(sketch, "E52", {"start": v(-32.36, 32.36) * mm, "end": v(32.36, -32.36) * mm});
            skLineSegment(sketch, "E53", {"start": v(32.36, 32.36) * mm, "end": v(-32.36, -32.36) * mm});
            skSolve(sketch);
        }
        {
            var Q0;
            Q0=qCreatedBy(makeId("Front.planeOp"),FACE);
            var sketch = newSketch(context, id + "F48", { "sketchPlane" : qUnion([Q0])});
            skLineSegment(sketch, "E54.0", {"start": v(32.36, -32.36) * mm, "end": v(-32.36, -32.36) * mm});
            skLineSegment(sketch, "E55", {"start": v(0, -32.36) * mm, "end": v(0, -52.36) * mm});
            skLineSegment(sketch, "E56", {"start": v(-20, -52.36) * mm, "end": v(20, -52.36) * mm});
            skSolve(sketch);
        }
        {
            var Q1;
            {var subQ0=sQuery(id+"F47.wireOp",EDGE,"E50.0");Q1=makeQuery(id+"F47.imprint","IMPRINT",FACE,{"disambiguationData":[TD([[makeQuery(id+"F47.imprint","IMPRINT",EDGE,{"derivedFrom":subQ0}),-1.0]])]});}
            var Q2;
            Q2=sQuery(id+"F48.wireOp",VERTEX,"E56.start");
            loft(context, id + "F49", {"operationType" : NewBodyOperationType.ADD, "sheetProfilesArray" : [{ "sheetProfileEntities" : qUnion([Q1]) }, { "sheetProfileEntities" : qUnion([Q2]) }]});
        }
        {
            var Q1;
            {var subQ0=sQuery(id+"F47.wireOp",EDGE,"E49.0");Q1=makeQuery(id+"F47.imprint","IMPRINT",FACE,{"disambiguationData":[TD([[makeQuery(id+"F47.imprint","IMPRINT",EDGE,{"derivedFrom":subQ0}),1.0]])]});}
            var Q2;
            Q2=sQuery(id+"F48.wireOp",VERTEX,"E56.end");
            loft(context, id + "F50", {"operationType" : NewBodyOperationType.ADD, "sheetProfilesArray" : [{ "sheetProfileEntities" : qUnion([Q1]) }, { "sheetProfileEntities" : qUnion([Q2]) }]});
        }
        {
            var Q1;
            {var subQ0=sQuery(id+"F47.wireOp",EDGE,"E51.0");Q1=makeQuery(id+"F47.imprint","IMPRINT",FACE,{"disambiguationData":[TD([[makeQuery(id+"F47.imprint","IMPRINT",EDGE,{"derivedFrom":subQ0}),1.0]])]});}
            var Q2;
            Q2=sQuery(id+"F48.wireOp",VERTEX,"E55.end");
            loft(context, id + "F51", {"operationType" : NewBodyOperationType.ADD, "sheetProfilesArray" : [{ "sheetProfileEntities" : qUnion([Q1]) }, { "sheetProfileEntities" : qUnion([Q2]) }]});
        }
        {
            var Q1;
            {var subQ0=sQuery(id+"F47.wireOp",EDGE,"E48.0");Q1=makeQuery(id+"F47.imprint","IMPRINT",FACE,{"disambiguationData":[TD([[makeQuery(id+"F47.imprint","IMPRINT",EDGE,{"derivedFrom":subQ0}),-1.0]])]});}
            var Q2;
            Q2=sQuery(id+"F48.wireOp",VERTEX,"E56.end");
            loft(context, id + "F52", {"operationType" : NewBodyOperationType.ADD, "sheetProfilesArray" : [{ "sheetProfileEntities" : qUnion([Q1]) }, { "sheetProfileEntities" : qUnion([Q2]) }]});
        }
        {
            var Q1;
            Q1=makeQuery(id+"F51.opLoft","SWEPT_FACE",FACE,{"disambiguationData":[OSD([sQuery(id+"F47.wireOp",EDGE,"E50.0"),sQuery(id+"F47.wireOp",EDGE,"E51.0"),sQuery(id+"F47.wireOp",EDGE,"E52"),sQuery(id+"F47.wireOp",EDGE,"E53")])]});
            var Q2;
            Q2=sQuery(id+"F48.wireOp",VERTEX,"E56.start");
            loft(context, id + "F53", {"operationType" : NewBodyOperationType.ADD, "sheetProfilesArray" : [{ "sheetProfileEntities" : qUnion([Q1]) }, { "sheetProfileEntities" : qUnion([Q2]) }]});
        }
        {
            var Q1;
            Q1=makeQuery(id+"F51.opLoft","SWEPT_FACE",FACE,{"disambiguationData":[OSD([sQuery(id+"F47.wireOp",EDGE,"E49.0"),sQuery(id+"F47.wireOp",EDGE,"E51.0"),sQuery(id+"F47.wireOp",EDGE,"E52"),sQuery(id+"F47.wireOp",EDGE,"E53")])]});
            var Q2;
            Q2=sQuery(id+"F48.wireOp",VERTEX,"E56.end");
            loft(context, id + "F54", {"operationType" : NewBodyOperationType.ADD, "sheetProfilesArray" : [{ "sheetProfileEntities" : qUnion([Q1]) }, { "sheetProfileEntities" : qUnion([Q2]) }]});
        }
        {
            var Q1;
            {var subQ0=sQuery(id+"F47.wireOp",EDGE,"E53");var subQ1=sQuery(id+"F47.wireOp",EDGE,"E52");Q1=makeQuery(id+"F52.boolean.opBoolean","MERGE",FACE,{"derivedFrom":[makeQuery(id+"F50.opLoft","SWEPT_FACE",FACE,{"disambiguationData":[OSD([sQuery(id+"F47.wireOp",EDGE,"E49.0"),sQuery(id+"F47.wireOp",EDGE,"E51.0"),subQ1,subQ0])]}),makeQuery(id+"F52.opLoft","SWEPT_FACE",FACE,{"disambiguationData":[OSD([sQuery(id+"F47.wireOp",EDGE,"E48.0"),sQuery(id+"F47.wireOp",EDGE,"E50.0"),subQ1,subQ0])]})]});}
            var Q2;
            Q2=sQuery(id+"F48.wireOp",VERTEX,"E56.start");
            loft(context, id + "F55", {"operationType" : NewBodyOperationType.ADD, "sheetProfilesArray" : [{ "sheetProfileEntities" : qUnion([Q1]) }, { "sheetProfileEntities" : qUnion([Q2]) }]});
        }
    });
